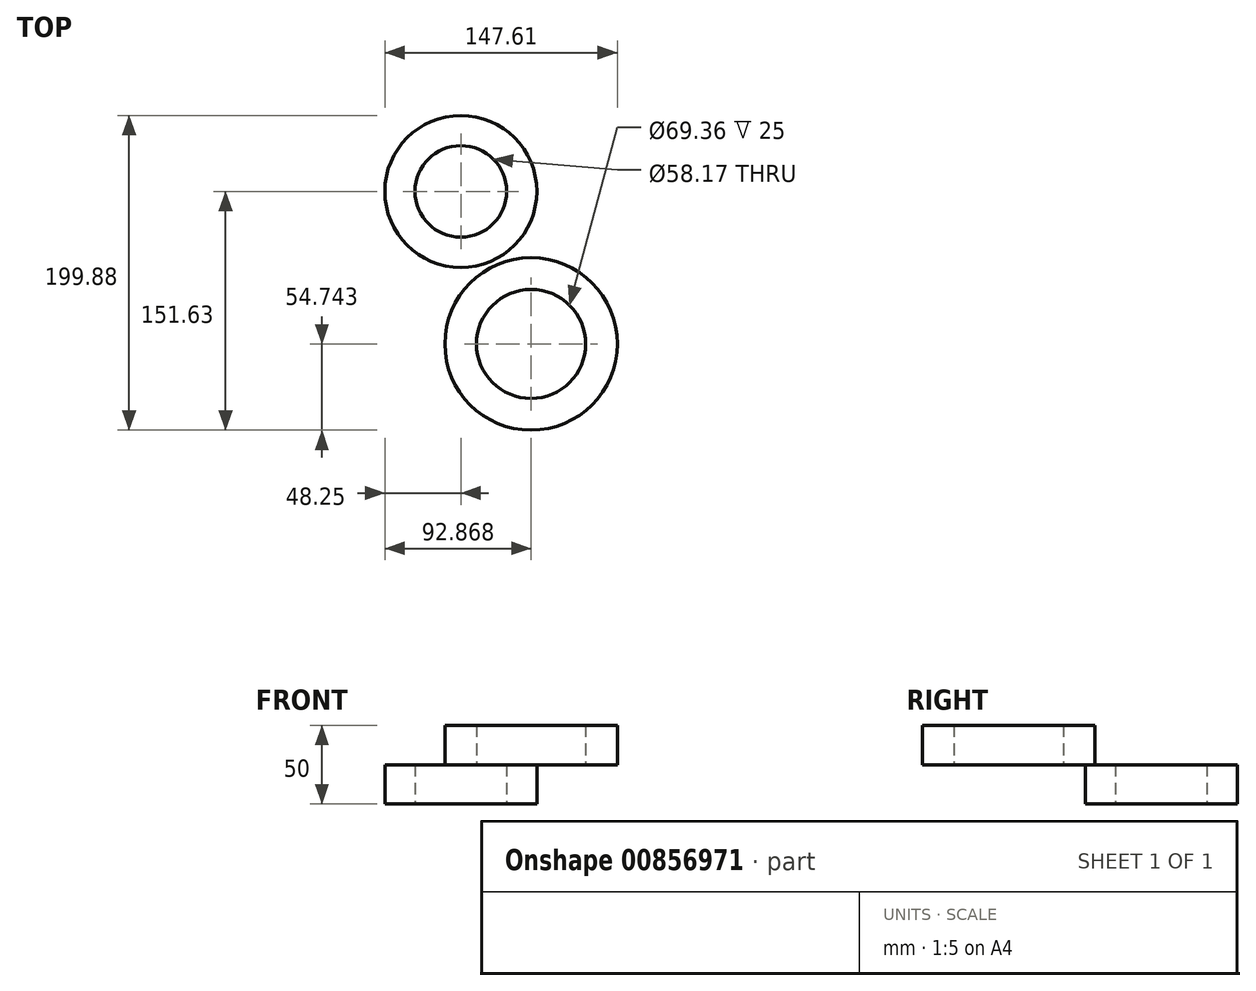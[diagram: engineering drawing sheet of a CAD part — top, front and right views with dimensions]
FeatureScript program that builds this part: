
annotation { "Feature Type Name" : "Feature", "Feature Type Description" : "" }
export const myFeature = defineFeature(function(context is Context, id is Id, definition is map)
    precondition{}
    {
        {
            var Q0;
            Q0=qCreatedBy(makeId("Top.planeOp"),FACE);
            var sketch = newSketch(context, id + "F0", { "sketchPlane" : qUnion([Q0])});
            skCircle(sketch, "E0", {"center": v(0, 0) * mm, "radius": 29.09 * mm});
            skCircle(sketch, "E1", {"center": v(0, 0) * mm, "radius": 48.25 * mm});
            skCircle(sketch, "E2", {"center": v(0, 0) * mm, "radius": 10.72 * mm});
            skCircle(sketch, "E3", {"center": v(0, 0) * mm, "radius": 18.76 * mm});
            skLineSegment(sketch, "E4", {"start": v(0, 10.72) * mm, "end": v(0, 18.76) * mm});
            skLineSegment(sketch, "E5", {"start": v(-10.72, 0) * mm, "end": v(-18.76, 0) * mm});
            skLineSegment(sketch, "E6", {"start": v(10.72, 0) * mm, "end": v(18.76, 0) * mm});
            skLineSegment(sketch, "E7", {"start": v(0, -10.72) * mm, "end": v(0, -18.76) * mm});
            skLineSegment(sketch, "E8", {"start": v(0, 29.09) * mm, "end": v(0, 48.25) * mm});
            skLineSegment(sketch, "E9", {"start": v(29.09, 0) * mm, "end": v(48.25, 0) * mm});
            skLineSegment(sketch, "E10", {"start": v(0, -29.09) * mm, "end": v(0, -48.25) * mm});
            skLineSegment(sketch, "E11", {"start": v(-29.09, 0) * mm, "end": v(-48.25, 0) * mm});
            skSolve(sketch);
        }
        {
            var Q0;
            Q0 = qSketchRegion(id + "F0", true);
            extrude(context, id + "F1", {"entities" : qUnion([Q0]), "depth" : 25 * mm, "offsetDistance" : 25 * mm});
        }
        {
            var Q0;
            Q0=makeQuery(id+"F1.opExtrude","CAP_FACE",FACE,{"disambiguationData":[OSD([sQuery(id+"F0.wireOp",EDGE,"E0"),sQuery(id+"F0.wireOp",EDGE,"E1")])],"isStart":false});
            var sketch = newSketch(context, id + "F2", { "sketchPlane" : qUnion([Q0])});
            skCircle(sketch, "E12", {"center": v(44.62, -96.89) * mm, "radius": 34.68 * mm});
            skCircle(sketch, "E13", {"center": v(44.62, -96.89) * mm, "radius": 54.75 * mm});
            skLineSegment(sketch, "E14", {"start": v(62.53, -148.62) * mm, "end": v(20.99, -43.45) * mm});
            skLineSegment(sketch, "E15", {"start": v(-5.23, -119.52) * mm, "end": v(-46.74, -12) * mm});
            skLineSegment(sketch, "E16", {"start": v(32.4, -43.52) * mm, "end": v(-9.62, 47.28) * mm});
            skLineSegment(sketch, "E17", {"start": v(98.33, -86.3) * mm, "end": v(42.96, 21.97) * mm});
            skSolve(sketch);
        }
        {
            var Q0;
            Q0 = qSketchRegion(id + "F2", true);
            extrude(context, id + "F3", {"entities" : qUnion([Q0]), "depth" : 25 * mm, "offsetDistance" : 25 * mm});
        }
    });
